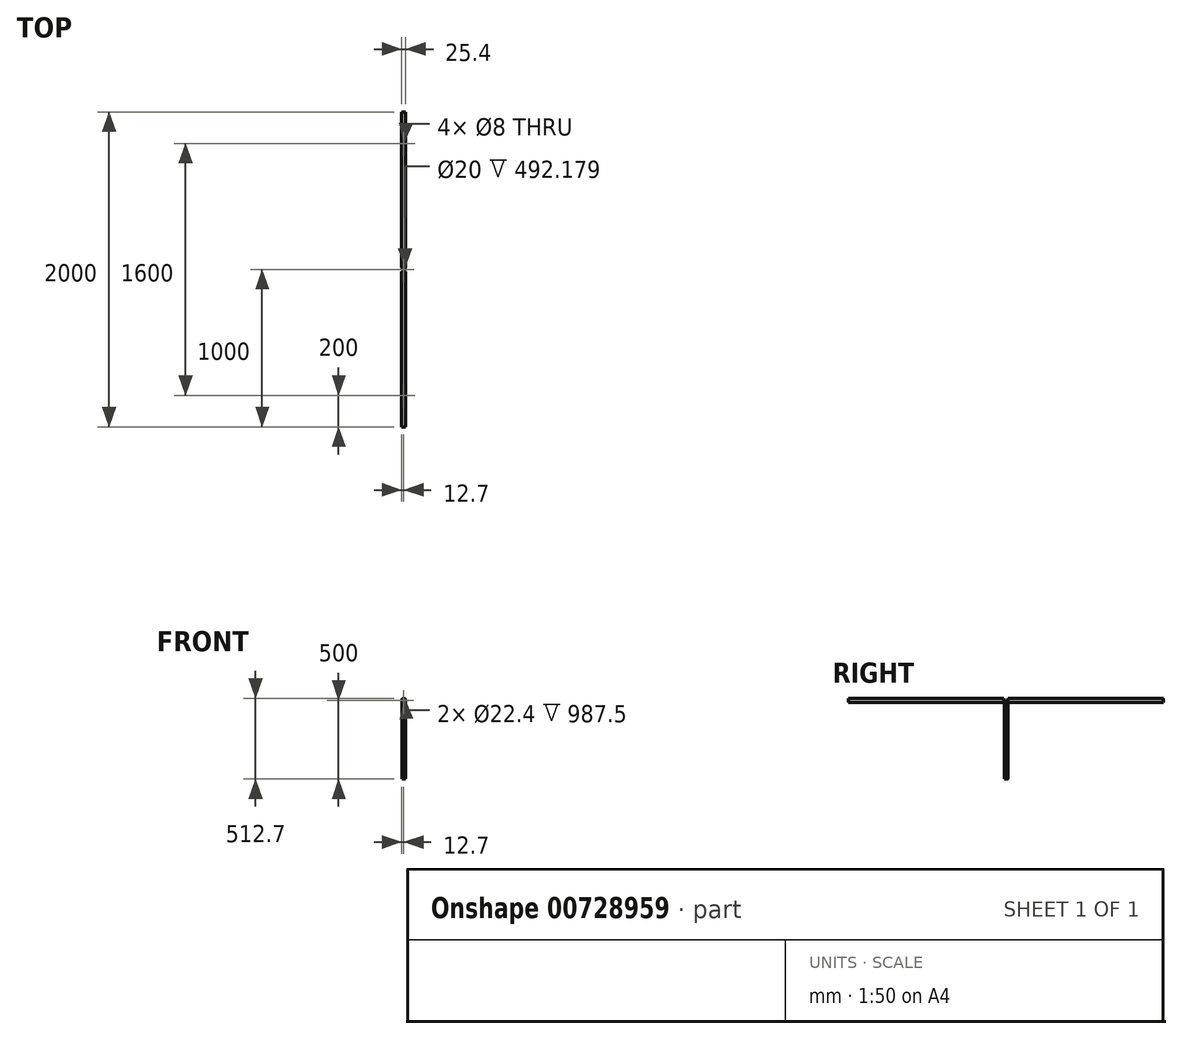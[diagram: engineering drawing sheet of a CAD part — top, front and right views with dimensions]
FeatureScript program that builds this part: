
annotation { "Feature Type Name" : "Feature", "Feature Type Description" : "" }
export const myFeature = defineFeature(function(context is Context, id is Id, definition is map)
    precondition{}
    {
        {
            var Q0;
            Q0=qCreatedBy(makeId("Front.planeOp"),FACE);
            var sketch = newSketch(context, id + "F0", { "sketchPlane" : qUnion([Q0])});
            skCircle(sketch, "E0", {"center": v(0, 0) * mm, "radius": 12.7 * mm});
            skCircle(sketch, "E1", {"center": v(0, 0) * mm, "radius": 11.2 * mm});
            skSolve(sketch);
        }
        {
            var Q0;
            Q0 = qSketchRegion(id + "F0", true);
            extrude(context, id + "F1", {"entities" : qUnion([Q0]), "endBound" : BoundingType.SYMMETRIC, "depth" : 2000 * mm, "offsetDistance" : 25 * mm});
        }
        {
            var Q0;
            Q0=qCreatedBy(makeId("Top.planeOp"),FACE);
            var sketch = newSketch(context, id + "F2", { "sketchPlane" : qUnion([Q0])});
            skCircle(sketch, "E2", {"center": v(0, 0) * mm, "radius": 11.2 * mm});
            skCircle(sketch, "E3", {"center": v(0, 0) * mm, "radius": 10 * mm});
            skSolve(sketch);
        }
        {
            var Q0;
            Q0 = qSketchRegion(id + "F2", true);
            extrude(context, id + "F3", {"entities" : qUnion([Q0]), "oppositeDirection" : true, "depth" : 500 * mm, "offsetDistance" : 25 * mm});
        }
        {
            var Q0;
            Q0=qCreatedBy(makeId("Front.planeOp"),FACE);
            var sketch = newSketch(context, id + "F4", { "sketchPlane" : qUnion([Q0])});
            skCircle(sketch, "E4", {"center": v(0, 0) * mm, "radius": 12.7 * mm});
            skSolve(sketch);
        }
        {
            var Q0;
            Q0 = qSketchRegion(id + "F4", true);
            extrude(context, id + "F5", {"entities" : qUnion([Q0]), "operationType" : NewBodyOperationType.REMOVE, "endBound" : BoundingType.SYMMETRIC, "oppositeDirection" : true, "depth" : 25 * mm, "offsetDistance" : 25 * mm});
        }
        {
            var Q0;
            Q0=qCreatedBy(makeId("Top.planeOp"),FACE);
            var sketch = newSketch(context, id + "F6", { "sketchPlane" : qUnion([Q0])});
            skCircle(sketch, "E5", {"center": v(0, 0) * mm, "radius": 4 * mm});
            skCircle(sketch, "E6", {"center": v(0, 800) * mm, "radius": 4 * mm});
            skCircle(sketch, "E7", {"center": v(0, -800) * mm, "radius": 4 * mm});
            skSolve(sketch);
        }
        {
            var Q0;
            Q0 = qSketchRegion(id + "F6", true);
            extrude(context, id + "F7", {"entities" : qUnion([Q0]), "operationType" : NewBodyOperationType.REMOVE, "endBound" : BoundingType.SYMMETRIC, "oppositeDirection" : true, "depth" : 30 * mm, "offsetDistance" : 25 * mm});
        }
    });
